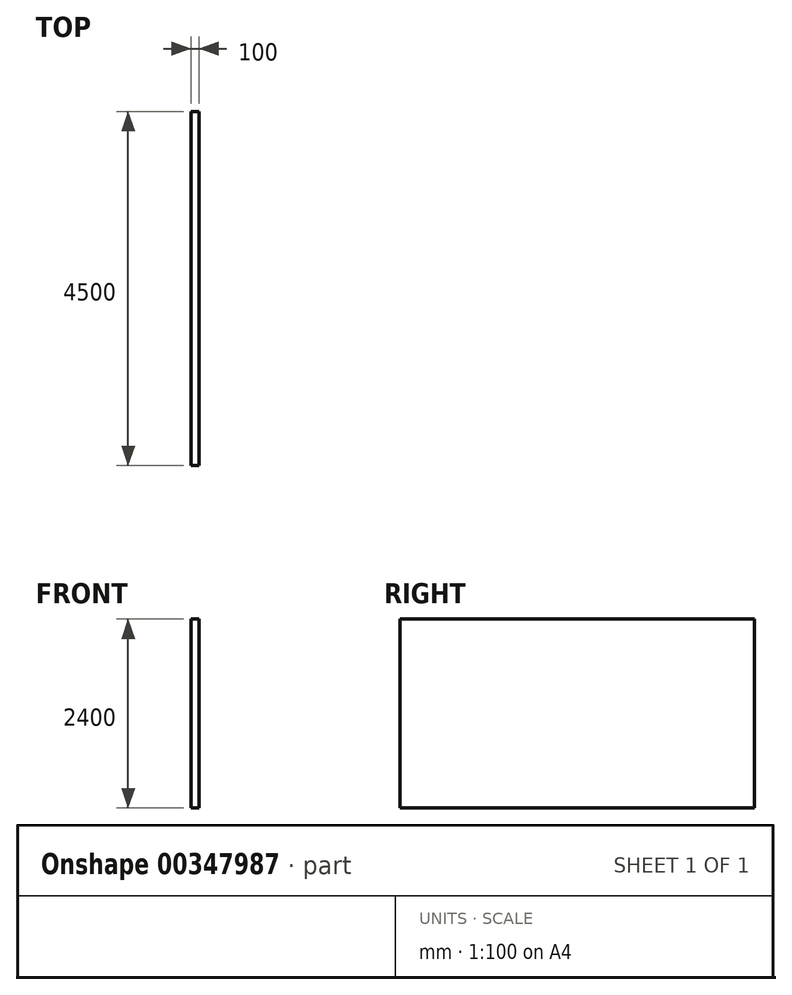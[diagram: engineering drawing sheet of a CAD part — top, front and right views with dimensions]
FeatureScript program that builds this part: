
annotation { "Feature Type Name" : "Feature", "Feature Type Description" : "" }
export const myFeature = defineFeature(function(context is Context, id is Id, definition is map)
    precondition{}
    {
        {
            var Q0;
            Q0=qCreatedBy(makeId("Right.planeOp"),FACE);
            var sketch = newSketch(context, id + "F0", { "sketchPlane" : qUnion([Q0])});
            skLineSegment(sketch, "E0.bottom", {"start": v(0, 0) * mm, "end": v(4500, 0) * mm});
            skLineSegment(sketch, "E0.top", {"start": v(0, 2400) * mm, "end": v(4500, 2400) * mm});
            skLineSegment(sketch, "E0.left", {"start": v(0, 0) * mm, "end": v(0, 2400) * mm});
            skLineSegment(sketch, "E0.right", {"start": v(4500, 0) * mm, "end": v(4500, 2400) * mm});
            skSolve(sketch);
        }
        {
            var Q0;
            Q0=makeQuery(id+"F0.imprint","IMPRINT",FACE,{"disambiguationData":[TD([[makeQuery(id+"F0.imprint","IMPRINT",EDGE,{"derivedFrom":sQuery(id+"F0.wireOp",EDGE,"E0.bottom")}),1.0]])]});
            extrude(context, id + "F1", {"entities" : qUnion([Q0]), "oppositeDirection" : true, "depth" : 100 * mm});
        }
    });
